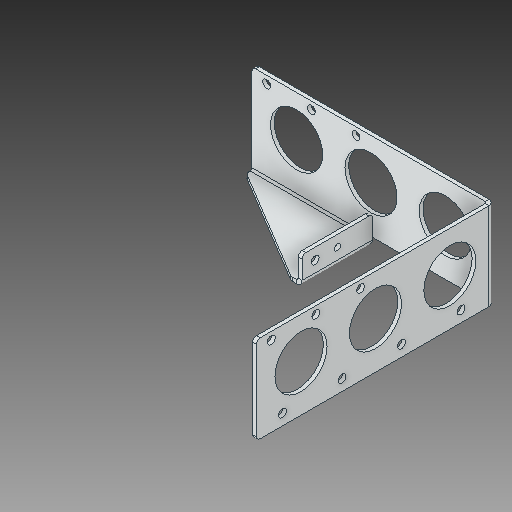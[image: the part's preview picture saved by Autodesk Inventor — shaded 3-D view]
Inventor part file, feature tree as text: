
AUTODESK INVENTOR PART (.ipt)
format: ipt  version: 2019 (Build 230136000, 136)  size: 165,888 bytes
history: native  units: in
note: dims shown in document units (in); Inventor stores cm internally (conversion verified against a paired STEP export)
features: fillet x1
ambient origin geometry x8: Origin, YZ Plane, XZ Plane, XY Plane, X Axis, Y Axis, Z Axis, Center Point
bodies: Solid1 (feature_tree)
feature tree (1):
  fillet  "Fillet1"  [1 undecoded]
note: 1 required parameter value undecoded (feature->parameter linkage not recoverable at this tier; creation-order binding heuristic only, values carry confidence <= 0.55)
